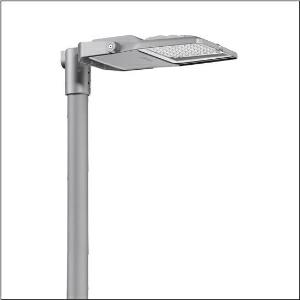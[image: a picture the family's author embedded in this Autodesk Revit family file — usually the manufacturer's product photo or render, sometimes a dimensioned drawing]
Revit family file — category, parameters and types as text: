
# Revit family: floodlight_fl_21_iq_mini___pl52_5xa7771b4d3a_0091
name_source: partatom
category: Lighting Fixtures
units: mm (PartAtom-declared; Revit-internal decimal feet)

## family parameters
Cut with Voids When Loaded = No
Host = Face
Light Source = No
Part Type = Normal
Room Calculation Point = No
Round Connector Dimension = Use Diameter
Shared = No

## types (1)
- --- (1 x LED, 6490 lm, 45.5 W, 4000K)
    Apparent Load = 46 VA
    CIE Flux Codes = 26 60 98 100 100
    Color Rendering = 70
    Color Temperature = 4000K
    Default Elevation = 1800 mm
    Description = Floodlight FL 21 iQ mini, floodlight, primary light control with lens, of PMMA, primary optical cover: protective disc, of toughened safety glass, transparent, light distribution: PL52, light emission: direct distribution, installation type: surface-mounted, LED, High Power LED, rated luminous flux: 6.490lm, luminous efficacy: 143lm/W, light colour: 740, colour temperature: 4000K, control: Auto-Match, Temp-Guard, Lumen-Switch, Night-Set, Smart-Wire, Light-Fading, Desk-Remote (wireless, voltage-free reading and setting of iQ features in the workshop via application-optimized NFC function/RFID function), optimised constant luminous flux control (CLO 2.0), with terminal, 6-pole, mains connection: 220..240V, AC, 50/60Hz, start of lifetime: 46W, end of service life: 48W, reduction: 22W, luminaire housing, of diecast aluminium, powder-coated, Siteco® metallic grey (DB 702S), corrosivity category C5 mid according to DIN EN ISO 12944, sealing non-destructively replaceable, please order mast flange separately, mast bracket, of steel, galvanised, powder-coated, Siteco® metallic grey (DB 702S), protection rating (complete): IP66, insulation class (complete): insulation class II (safety insulation), certification: CE, ENEC, VDE, protection symbol: D, impact resistance: IK08, permissible operating ambient temperature: -40..+40°C, permissible operating ambient temperature for outdoor applications: -40..+50°C, standard: DIN EN 12944, LABS conformity tested according to VDMA 24364:2018-05, packaging unit: 1 piece

Light Distribution: PL52
    Height = 70 mm
    Lamp = 1 x LED
    Lamp Light Flux = 6490 lm
    Lamp Power = 45.5 W
    Lamp count = 1
    Length = 485 mm
    Luminous efficacy = 143 lm/W
    Manufacturer = Siteco
    ModVariant = No
    Model = 5XA7771B4D3A
    Number of Poles = 1
    OnlyDefault = Yes
    Power Factor = 1
    Product Name = Floodlight FL 21 iQ mini | PL52
    Product group = floodlight | pylon annexe
    ProductGroupID = 6200
    Protection Class = Protection class II
    Protection Degree = IP 66
    RLX_Detail_Level = 1
    RLX_Emergency_Light_Flux = 0 lm
    RLX_Emergency_Type = 0
    RLX_Emergency_Type_DB = No
    RlxData = <blob elided: 101357 chars, md5=5f44360e>
    Socket = socket
    Standby Power = 0 W
    System Light Flux = 6490 lm
    System Power = 46 W
    Type Comments = factory setting: luminous flux: 100 % | dim-lin: 254 | 463 mA
    Type Image = l_1007125.jpg
    URL = http://relux.com
    VarID = @adj_097287
    Voltage = 0 V
    Weight = 0.00 kg
    Width = 337 mm

## geometry (parser evidence)
native form markers: Blend x4, Sweep x11
no freeform markers — native parametric forms only
